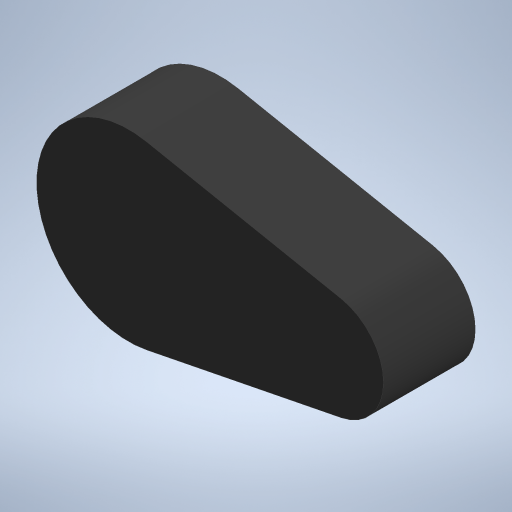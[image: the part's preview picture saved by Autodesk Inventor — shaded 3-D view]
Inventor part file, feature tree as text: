
AUTODESK INVENTOR PART (.ipt)
format: ipt  version: 2023 (Build 270158000, 158)  size: 201,216 bytes
history: native  units: in
note: dims shown in document units (in); Inventor stores cm internally (conversion verified against a paired STEP export)
features: extrude x1, sketch x1
ambient origin geometry x8: Origin, YZ Plane, XZ Plane, XY Plane, X Axis, Y Axis, Z Axis, Center Point
bodies: Solid1 (feature_tree)
feature tree (2):
  extrude  "Extrusion1"  Depth=1.378in
  sketch  "Sketch1"  dims[d0=2.7559in d2=1.5748in d3=0.0in d4=5.2005in d5=1.378in d6=0.0in]
